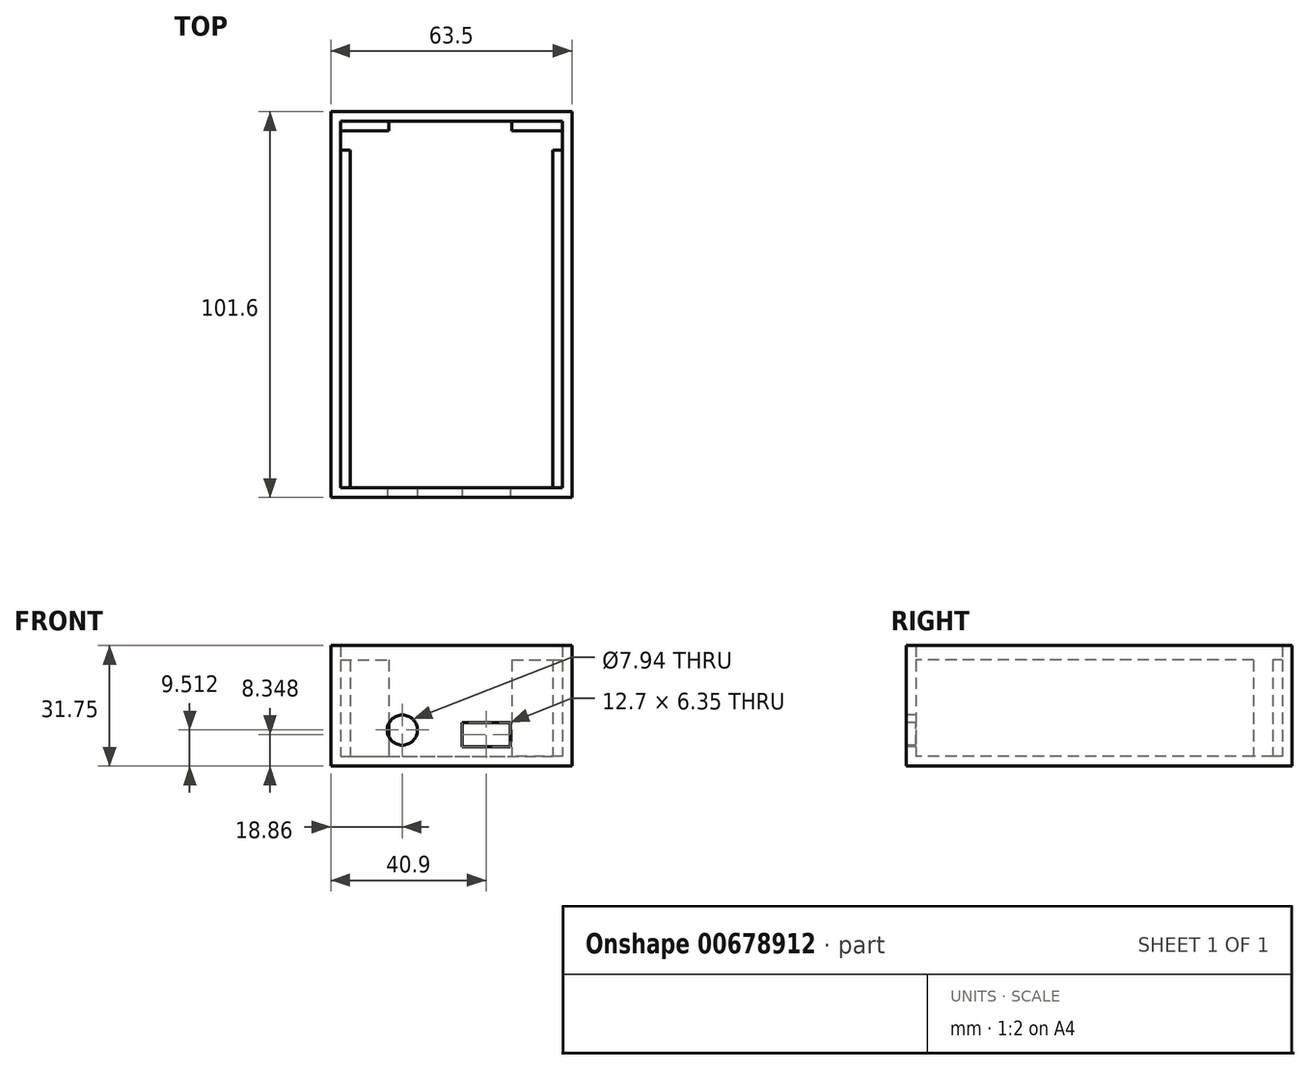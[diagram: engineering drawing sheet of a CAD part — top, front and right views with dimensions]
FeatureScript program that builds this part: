
annotation { "Feature Type Name" : "Feature", "Feature Type Description" : "" }
export const myFeature = defineFeature(function(context is Context, id is Id, definition is map)
    precondition{}
    {
        {
            var Q0;
            Q0=qCreatedBy(makeId("Top.planeOp"),FACE);
            var sketch = newSketch(context, id + "F0", { "sketchPlane" : qUnion([Q0])});
            skLineSegment(sketch, "E0.bottom", {"start": v(-31.75, 50.8) * mm, "end": v(31.75, 50.8) * mm});
            skLineSegment(sketch, "E0.top", {"start": v(-31.75, -50.8) * mm, "end": v(31.75, -50.8) * mm});
            skLineSegment(sketch, "E0.left", {"start": v(-31.75, 50.8) * mm, "end": v(-31.75, -50.8) * mm});
            skLineSegment(sketch, "E0.right", {"start": v(31.75, 50.8) * mm, "end": v(31.75, -50.8) * mm});
            skPoint(sketch, "E0.middle", {"position": v(0, 0) * mm});
            skLineSegment(sketch, "E1.top", {"start": v(-31.75, 48.26) * mm, "end": v(31.75, 48.26) * mm});
            skLineSegment(sketch, "E1.left", {"start": v(-31.75, 50.8) * mm, "end": v(-31.75, 48.26) * mm});
            skLineSegment(sketch, "E1.right", {"start": v(31.75, 50.8) * mm, "end": v(31.75, 48.26) * mm});
            skLineSegment(sketch, "E2.bottom", {"start": v(31.75, 50.8) * mm, "end": v(29.2, 50.8) * mm});
            skLineSegment(sketch, "E2.top", {"start": v(31.75, -50.8) * mm, "end": v(29.21, -50.8) * mm});
            skLineSegment(sketch, "E2.right", {"start": v(29.2, 50.8) * mm, "end": v(29.21, -50.8) * mm});
            skLineSegment(sketch, "E3.top", {"start": v(-31.75, -48.26) * mm, "end": v(31.75, -48.26) * mm});
            skLineSegment(sketch, "E3.left", {"start": v(-31.75, -50.8) * mm, "end": v(-31.75, -48.26) * mm});
            skLineSegment(sketch, "E3.right", {"start": v(31.75, -50.8) * mm, "end": v(31.75, -48.26) * mm});
            skLineSegment(sketch, "E4.bottom", {"start": v(-31.75, -50.8) * mm, "end": v(-29.2, -50.8) * mm});
            skLineSegment(sketch, "E4.top", {"start": v(-31.75, 50.8) * mm, "end": v(-29.21, 50.8) * mm});
            skLineSegment(sketch, "E4.left", {"start": v(-31.75, -50.8) * mm, "end": v(-31.75, 50.8) * mm});
            skLineSegment(sketch, "E4.right", {"start": v(-29.2, -50.8) * mm, "end": v(-29.21, 50.8) * mm});
            skSolve(sketch);
        }
        {
            var Q0;
            {var subQ0=sQuery(id+"F0.wireOp",EDGE,"E4.right");var subQ1=sQuery(id+"F0.wireOp",EDGE,"E1.top");var subQ2=makeQuery(id+"F0.imprint","INTERSECT",VERTEX,{"derivedFrom":[subQ1,subQ0]});Q0=makeQuery(id+"F0.imprint","IMPRINT",FACE,{"disambiguationData":[TD([[makeQuery(id+"F0.imprint","IMPRINT",EDGE,{"disambiguationData":[TD([[subQ2,-1.0]])],"derivedFrom":subQ1}),-1.0]])]});}
            extrude(context, id + "F1", {"entities" : qUnion([Q0]), "depth" : 2.54 * mm, "offsetDistance" : 25.4 * mm});
        }
        {
            var Q0;
            Q0 = qSketchRegion(id + "F0", true);
            extrude(context, id + "F2", {"entities" : qUnion([Q0]), "operationType" : NewBodyOperationType.ADD, "depth" : 31.75 * mm, "offsetDistance" : 25.4 * mm});
        }
        {
            var Q0;
            Q0=makeQuery(id+"F1.opExtrude","CAP_FACE",FACE,{"disambiguationData":[OSD([sQuery(id+"F0.wireOp",EDGE,"E1.top"),sQuery(id+"F0.wireOp",EDGE,"E2.right"),sQuery(id+"F0.wireOp",EDGE,"E3.top"),sQuery(id+"F0.wireOp",EDGE,"E4.right")])],"isStart":false});
            var sketch = newSketch(context, id + "F3", { "sketchPlane" : qUnion([Q0])});
            skLineSegment(sketch, "E5.bottom", {"start": v(-29.21, 48.26) * mm, "end": v(-16.51, 48.26) * mm});
            skLineSegment(sketch, "E5.top", {"start": v(-29.21, 45.72) * mm, "end": v(-16.51, 45.72) * mm});
            skLineSegment(sketch, "E5.left", {"start": v(-29.21, 48.26) * mm, "end": v(-29.21, 45.72) * mm});
            skLineSegment(sketch, "E5.right", {"start": v(-16.51, 48.26) * mm, "end": v(-16.51, 45.72) * mm});
            skLineSegment(sketch, "E6.bottom", {"start": v(-29.21, 48.26) * mm, "end": v(-26.67, 48.26) * mm});
            skLineSegment(sketch, "E6.top", {"start": v(-29.21, 35.56) * mm, "end": v(-26.67, 35.56) * mm});
            skLineSegment(sketch, "E6.left", {"start": v(-29.21, 48.26) * mm, "end": v(-29.21, 35.56) * mm});
            skLineSegment(sketch, "E6.right", {"start": v(-26.67, 48.26) * mm, "end": v(-26.67, 35.56) * mm});
            skLineSegment(sketch, "E7.bottom", {"start": v(29.2, 48.26) * mm, "end": v(15.91, 48.26) * mm});
            skLineSegment(sketch, "E7.top", {"start": v(29.2, 45.72) * mm, "end": v(15.91, 45.72) * mm});
            skLineSegment(sketch, "E7.left", {"start": v(29.2, 48.26) * mm, "end": v(29.2, 45.72) * mm});
            skLineSegment(sketch, "E7.right", {"start": v(15.91, 48.26) * mm, "end": v(15.91, 45.72) * mm});
            skLineSegment(sketch, "E8.bottom", {"start": v(29.2, 48.26) * mm, "end": v(26.67, 48.26) * mm});
            skLineSegment(sketch, "E8.top", {"start": v(29.2, 35.56) * mm, "end": v(26.67, 35.56) * mm});
            skLineSegment(sketch, "E8.left", {"start": v(29.2, 48.26) * mm, "end": v(29.2, 35.56) * mm});
            skLineSegment(sketch, "E8.right", {"start": v(26.67, 48.26) * mm, "end": v(26.67, 35.56) * mm});
            skLineSegment(sketch, "E9.bottom", {"start": v(29.2, -48.26) * mm, "end": v(26.67, -48.26) * mm});
            skLineSegment(sketch, "E9.top", {"start": v(29.2, 40.64) * mm, "end": v(26.67, 40.64) * mm});
            skLineSegment(sketch, "E9.left", {"start": v(29.2, -48.26) * mm, "end": v(29.2, 40.64) * mm});
            skLineSegment(sketch, "E9.right", {"start": v(26.67, -48.26) * mm, "end": v(26.67, 40.64) * mm});
            skLineSegment(sketch, "E10.bottom", {"start": v(-29.2, -48.26) * mm, "end": v(-26.67, -48.26) * mm});
            skLineSegment(sketch, "E10.top", {"start": v(-29.21, 40.64) * mm, "end": v(-26.67, 40.64) * mm});
            skLineSegment(sketch, "E10.left", {"start": v(-29.2, -48.26) * mm, "end": v(-29.21, 40.64) * mm});
            skLineSegment(sketch, "E10.right", {"start": v(-26.67, -48.26) * mm, "end": v(-26.67, 40.64) * mm});
            skSolve(sketch);
        }
        {
            var Q0;
            {var subQ5=sQuery(id+"F3.wireOp",EDGE,"E6.top");Q0=makeQuery(id+"F3.imprint","IMPRINT",FACE,{"disambiguationData":[TD([[makeQuery(id+"F3.imprint","IMPRINT",EDGE,{"derivedFrom":subQ5}),1.0]])]});}
            var Q1;
            {var subQ5=sQuery(id+"F3.wireOp",EDGE,"E6.bottom");Q1=makeQuery(id+"F3.imprint","IMPRINT",FACE,{"disambiguationData":[TD([[makeQuery(id+"F3.imprint","IMPRINT",EDGE,{"derivedFrom":subQ5}),-1.0]])]});}
            var Q2;
            {var subQ0=sQuery(id+"F3.wireOp",EDGE,"E5.bottom");Q2=makeQuery(id+"F3.imprint","IMPRINT",FACE,{"disambiguationData":[TD([[makeQuery(id+"F3.imprint","IMPRINT",EDGE,{"derivedFrom":subQ0}),-1.0]])]});}
            var Q3;
            {var subQ0=sQuery(id+"F3.wireOp",EDGE,"E7.bottom");Q3=makeQuery(id+"F3.imprint","IMPRINT",FACE,{"disambiguationData":[TD([[makeQuery(id+"F3.imprint","IMPRINT",EDGE,{"derivedFrom":subQ0}),-1.0]])]});}
            var Q4;
            {var subQ5=sQuery(id+"F3.wireOp",EDGE,"E8.bottom");Q4=makeQuery(id+"F3.imprint","IMPRINT",FACE,{"disambiguationData":[TD([[makeQuery(id+"F3.imprint","IMPRINT",EDGE,{"derivedFrom":subQ5}),-1.0]])]});}
            var Q5;
            {var subQ5=sQuery(id+"F3.wireOp",EDGE,"E8.top");Q5=makeQuery(id+"F3.imprint","IMPRINT",FACE,{"disambiguationData":[TD([[makeQuery(id+"F3.imprint","IMPRINT",EDGE,{"derivedFrom":subQ5}),-1.0]])]});}
            var Q6;
            Q6=makeQuery(id+"F3.imprint","IMPRINT",FACE,{"disambiguationData":[TD([[makeQuery(id+"F3.imprint","IMPRINT",EDGE,{"derivedFrom":sQuery(id+"F3.wireOp",EDGE,"E9.bottom")}),1.0]])]});
            var Q7;
            Q7=makeQuery(id+"F3.imprint","IMPRINT",FACE,{"disambiguationData":[TD([[makeQuery(id+"F3.imprint","IMPRINT",EDGE,{"derivedFrom":sQuery(id+"F3.wireOp",EDGE,"E10.bottom")}),1.0]])]});
            extrude(context, id + "F4", {"entities" : qUnion([Q0, Q1, Q2, Q3, Q4, Q5, Q6, Q7]), "operationType" : NewBodyOperationType.ADD, "depth" : 25.4 * mm, "offsetDistance" : 25.4 * mm});
        }
        {
            var Q0;
            Q0=makeQuery(id+"F2.opExtrude","SWEPT_FACE",FACE,{"disambiguationData":[OSD([sQuery(id+"F0.wireOp",EDGE,"E0.top"),sQuery(id+"F0.wireOp",EDGE,"E4.bottom")])]});
            var sketch = newSketch(context, id + "F5", { "sketchPlane" : qUnion([Q0])});
            skLineSegment(sketch, "E11.bottom", {"start": v(2.8, 11.52) * mm, "end": v(15.5, 11.52) * mm});
            skLineSegment(sketch, "E11.top", {"start": v(2.8, 5.17) * mm, "end": v(15.5, 5.17) * mm});
            skLineSegment(sketch, "E11.left", {"start": v(2.8, 11.52) * mm, "end": v(2.8, 5.17) * mm});
            skLineSegment(sketch, "E11.right", {"start": v(15.5, 11.52) * mm, "end": v(15.5, 5.17) * mm});
            skPoint(sketch, "E11.middle", {"position": v(9.15, 8.35) * mm});
            skCircle(sketch, "E12", {"center": v(-12.9, 9.51) * mm, "radius": 3.97 * mm});
            skSolve(sketch);
        }
        {
            var Q0;
            Q0=makeQuery(id+"F5.imprint","IMPRINT",FACE,{"disambiguationData":[TD([[makeQuery(id+"F5.imprint","IMPRINT",EDGE,{"derivedFrom":sQuery(id+"F5.wireOp",EDGE,"E12")}),1.0]])]});
            var Q1;
            Q1=makeQuery(id+"F5.imprint","IMPRINT",FACE,{"disambiguationData":[TD([[makeQuery(id+"F5.imprint","IMPRINT",EDGE,{"derivedFrom":sQuery(id+"F5.wireOp",EDGE,"E11.bottom")}),-1.0]])]});
            extrude(context, id + "F6", {"entities" : qUnion([Q0, Q1]), "operationType" : NewBodyOperationType.REMOVE, "oppositeDirection" : true, "depth" : 25.4 * mm, "offsetDistance" : 25.4 * mm});
        }
    });
